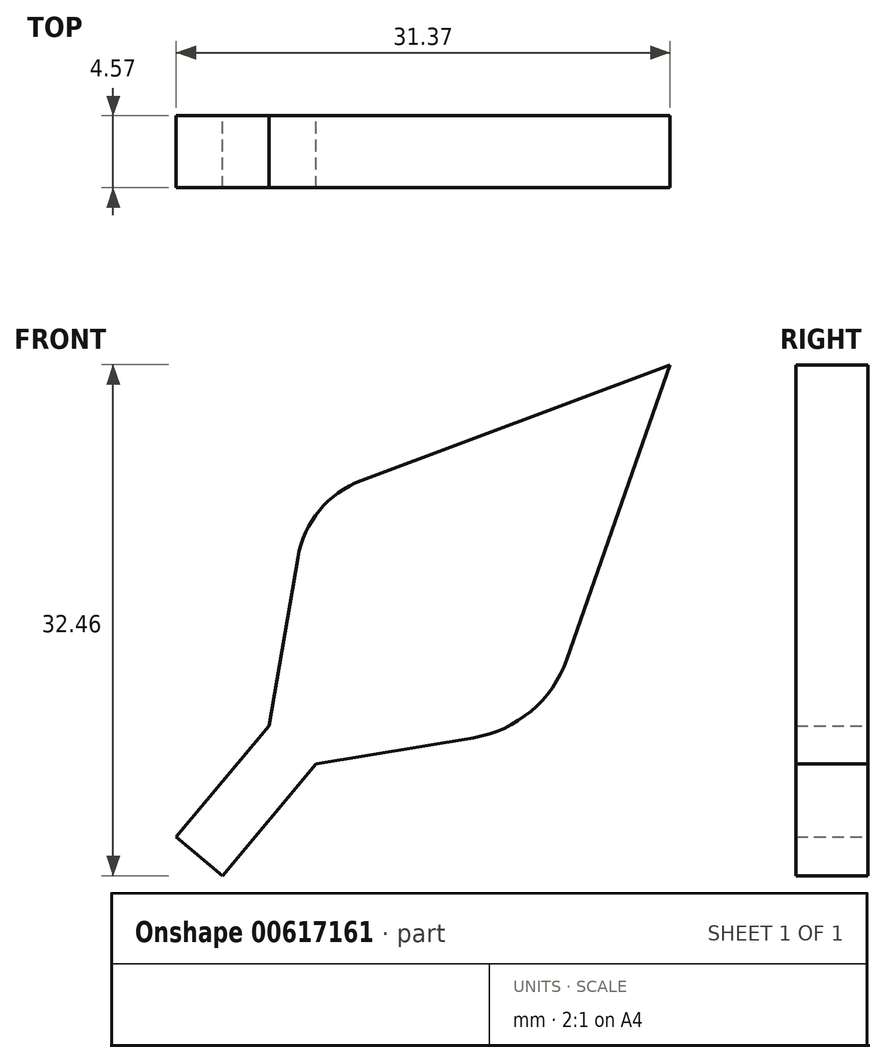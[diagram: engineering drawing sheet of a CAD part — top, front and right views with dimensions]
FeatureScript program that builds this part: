
annotation { "Feature Type Name" : "Feature", "Feature Type Description" : "" }
export const myFeature = defineFeature(function(context is Context, id is Id, definition is map)
    precondition{}
    {
        {
            var Q0;
            Q0=qCreatedBy(makeId("Front.planeOp"),FACE);
            var sketch = newSketch(context, id + "F0", { "sketchPlane" : qUnion([Q0])});
            skLineSegment(sketch, "E0", {"start": v(0, 0) * mm, "end": v(-5.9, -7.05) * mm});
            skLineSegment(sketch, "E1", {"start": v(-5.9, -7.05) * mm, "end": v(-2.96, -9.51) * mm});
            skLineSegment(sketch, "E2", {"start": v(-2.96, -9.51) * mm, "end": v(2.98, -2.41) * mm});
            skLineSegment(sketch, "E3", {"start": v(2.98, -2.41) * mm, "end": v(0, 0) * mm});
            skLineSegment(sketch, "E4", {"start": v(0, 0) * mm, "end": v(1.83, 10.72) * mm});
            skLineSegment(sketch, "E5", {"start": v(25.47, 22.95) * mm, "end": v(5.86, 15.6) * mm});
            skLineSegment(sketch, "E6", {"start": v(2.98, -2.41) * mm, "end": v(12.98, -0.74) * mm});
            skLineSegment(sketch, "E7", {"start": v(18.92, 4.25) * mm, "end": v(25.47, 22.95) * mm});
            skPoint(sketch, "E8.visualSharp", {"position": v(2.45, 14.31) * mm});
            skArc(sketch, "E8.filletArc", {"start": v(5.86, 15.6) * mm, "mid": v(3.2, 13.7) * mm, "end": v(1.83, 10.72) * mm});
            skPoint(sketch, "E9.visualSharp", {"position": v(17.43, 0) * mm});
            skArc(sketch, "E9.filletArc", {"start": v(12.98, -0.74) * mm, "mid": v(16.63, 0.94) * mm, "end": v(18.92, 4.25) * mm});
            skSolve(sketch);
        }
        {
            var Q0;
            Q0=makeQuery(id+"F0.imprint","IMPRINT",FACE,{"disambiguationData":[TD([[makeQuery(id+"F0.imprint","IMPRINT",EDGE,{"derivedFrom":sQuery(id+"F0.wireOp",EDGE,"E3")}),-1.0]])]});
            var Q1;
            Q1=makeQuery(id+"F0.imprint","IMPRINT",FACE,{"disambiguationData":[TD([[makeQuery(id+"F0.imprint","IMPRINT",EDGE,{"derivedFrom":sQuery(id+"F0.wireOp",EDGE,"E0")}),1.0]])]});
            extrude(context, id + "F1", {"entities" : qUnion([Q0, Q1]), "depth" : 4.57 * mm, "offsetDistance" : 25.4 * mm});
        }
    });
